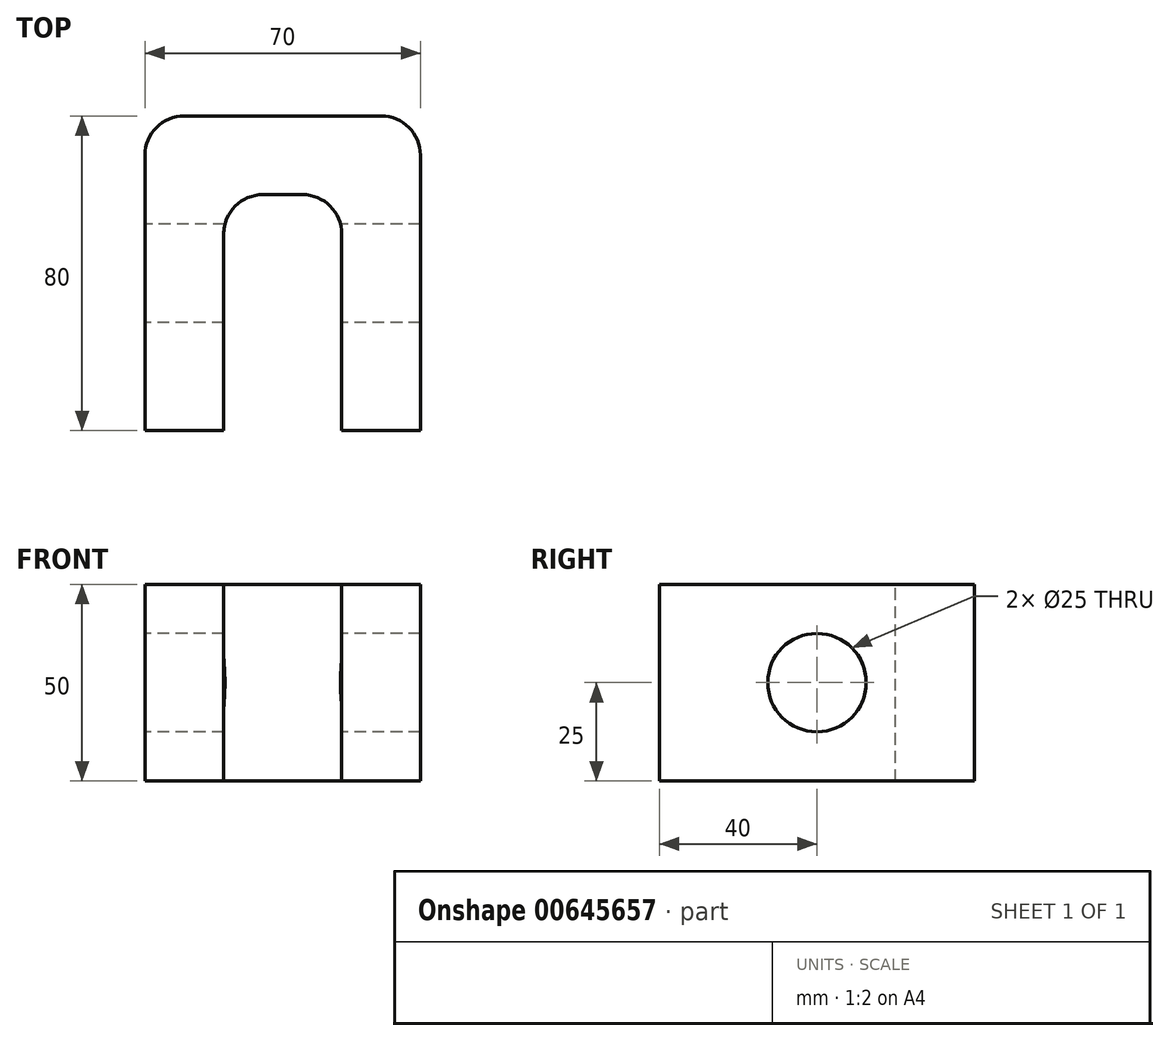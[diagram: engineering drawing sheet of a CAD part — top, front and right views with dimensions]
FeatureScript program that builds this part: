
annotation { "Feature Type Name" : "Feature", "Feature Type Description" : "" }
export const myFeature = defineFeature(function(context is Context, id is Id, definition is map)
    precondition{}
    {
        {
            var Q0;
            Q0=qCreatedBy(makeId("Top.planeOp"),FACE);
            var sketch = newSketch(context, id + "F0", { "sketchPlane" : qUnion([Q0])});
            skLineSegment(sketch, "E0.bottom", {"start": v(35, -40) * mm, "end": v(-35, -40) * mm});
            skLineSegment(sketch, "E0.top", {"start": v(35, 40) * mm, "end": v(-35, 40) * mm});
            skLineSegment(sketch, "E0.left", {"start": v(35, -40) * mm, "end": v(35, 40) * mm});
            skLineSegment(sketch, "E0.right", {"start": v(-35, -40) * mm, "end": v(-35, 40) * mm});
            skPoint(sketch, "E0.middle", {"position": v(0, 0) * mm});
            skSolve(sketch);
        }
        {
            var Q0;
            Q0=makeQuery(id+"F0.imprint","IMPRINT",FACE,{"disambiguationData":[TD([[makeQuery(id+"F0.imprint","IMPRINT",EDGE,{"derivedFrom":sQuery(id+"F0.wireOp",EDGE,"E0.bottom")}),-1.0]])]});
            extrude(context, id + "F1", {"entities" : qUnion([Q0]), "depth" : 50 * mm, "offsetDistance" : 25 * mm});
        }
        {
            var Q0;
            Q0=makeQuery(id+"F1.opExtrude","CAP_FACE",FACE,{"disambiguationData":[OSD([sQuery(id+"F0.wireOp",EDGE,"E0.bottom"),sQuery(id+"F0.wireOp",EDGE,"E0.top"),sQuery(id+"F0.wireOp",EDGE,"E0.left"),sQuery(id+"F0.wireOp",EDGE,"E0.right")])],"isStart":false});
            var sketch = newSketch(context, id + "F2", { "sketchPlane" : qUnion([Q0])});
            skLineSegment(sketch, "E1.bottom", {"start": v(-15, -40) * mm, "end": v(15, -40) * mm});
            skLineSegment(sketch, "E1.top", {"start": v(-15, 20) * mm, "end": v(15, 20) * mm});
            skLineSegment(sketch, "E1.left", {"start": v(-15, -40) * mm, "end": v(-15, 20) * mm});
            skLineSegment(sketch, "E1.right", {"start": v(15, -40) * mm, "end": v(15, 20) * mm});
            skSolve(sketch);
        }
        {
            var Q0;
            Q0=makeQuery(id+"F2.imprint","IMPRINT",FACE,{"disambiguationData":[TD([[makeQuery(id+"F2.imprint","IMPRINT",EDGE,{"derivedFrom":sQuery(id+"F2.wireOp",EDGE,"E1.bottom")}),-1.0]])]});
            extrude(context, id + "F3", {"entities" : qUnion([Q0]), "operationType" : NewBodyOperationType.REMOVE, "oppositeDirection" : true, "depth" : 64 * mm, "offsetDistance" : 25 * mm});
        }
        {
            var Q0;
            Q0=makeQuery(id+"F1.opExtrude","SWEPT_EDGE",EDGE,{"disambiguationData":[OSD([sQuery(id+"F0.wireOp",EDGE,"E0.top"),sQuery(id+"F0.wireOp",EDGE,"E0.left")])]});
            var Q1;
            Q1=makeQuery(id+"F1.opExtrude","SWEPT_EDGE",EDGE,{"disambiguationData":[OSD([sQuery(id+"F0.wireOp",EDGE,"E0.top"),sQuery(id+"F0.wireOp",EDGE,"E0.right")])]});
            var Q2;
            Q2=makeQuery(id+"F3.boolean.opBoolean","COPY",EDGE,{"derivedFrom":makeQuery(id+"F3.opExtrude","SWEPT_EDGE",EDGE,{"disambiguationData":[OSD([sQuery(id+"F2.wireOp",EDGE,"E1.top"),sQuery(id+"F2.wireOp",EDGE,"E1.left")])]})});
            var Q3;
            Q3=makeQuery(id+"F3.boolean.opBoolean","COPY",EDGE,{"derivedFrom":makeQuery(id+"F3.opExtrude","SWEPT_EDGE",EDGE,{"disambiguationData":[OSD([sQuery(id+"F2.wireOp",EDGE,"E1.top"),sQuery(id+"F2.wireOp",EDGE,"E1.right")])]})});
            fillet(context, id + "F4", {"entities" : qUnion([Q0, Q1, Q2, Q3]), "radius" : 10 * mm, "tangentPropagation" : true, "allowEdgeOverflow" : false});
        }
        {
            var Q0;
            Q0=makeQuery(id+"F1.opExtrude","SWEPT_FACE",FACE,{"disambiguationData":[OSD([sQuery(id+"F0.wireOp",EDGE,"E0.right")])]});
            var sketch = newSketch(context, id + "F5", { "sketchPlane" : qUnion([Q0])});
            skCircle(sketch, "E2", {"center": v(0, 25) * mm, "radius": 12.5 * mm});
            skSolve(sketch);
        }
        {
            var Q0;
            Q0=makeQuery(id+"F5.imprint","IMPRINT",FACE,{"disambiguationData":[TD([[makeQuery(id+"F5.imprint","IMPRINT",EDGE,{"derivedFrom":sQuery(id+"F5.wireOp",EDGE,"E2")}),1.0]])]});
            extrude(context, id + "F6", {"entities" : qUnion([Q0]), "operationType" : NewBodyOperationType.REMOVE, "oppositeDirection" : true, "depth" : 96.7 * mm, "offsetDistance" : 25 * mm});
        }
    });
